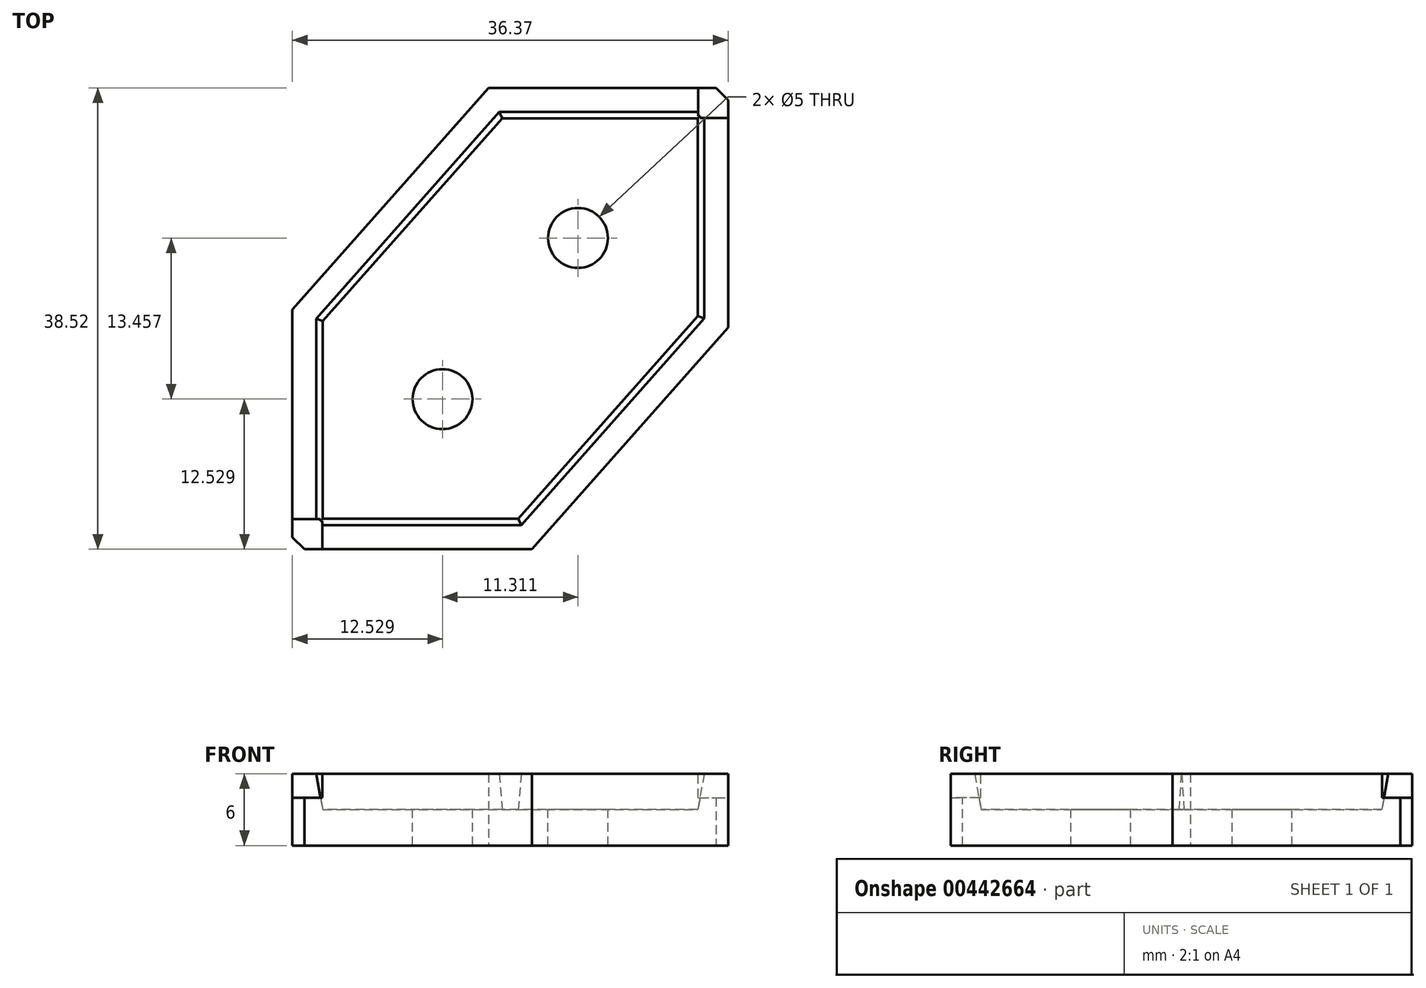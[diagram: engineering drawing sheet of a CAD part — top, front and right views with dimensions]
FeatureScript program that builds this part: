
annotation { "Feature Type Name" : "Feature", "Feature Type Description" : "" }
export const myFeature = defineFeature(function(context is Context, id is Id, definition is map)
    precondition{}
    {
        {
            var Q0;
            Q0=qCreatedBy(makeId("Top.planeOp"),FACE);
            var sketch = newSketch(context, id + "F0", { "sketchPlane" : qUnion([Q0])});
            skLineSegment(sketch, "E0.bottom", {"start": v(0, 0) * mm, "end": v(20, 0) * mm});
            skLineSegment(sketch, "E0.top", {"start": v(16.37, 38.52) * mm, "end": v(36.37, 38.52) * mm});
            skLineSegment(sketch, "E0.left", {"start": v(0, 0) * mm, "end": v(0, 20) * mm});
            skLineSegment(sketch, "E0.right", {"start": v(36.37, 18.52) * mm, "end": v(36.37, 38.52) * mm});
            skLineSegment(sketch, "E1", {"start": v(16.37, 38.52) * mm, "end": v(0, 20) * mm});
            skLineSegment(sketch, "E2", {"start": v(36.37, 18.52) * mm, "end": v(20, 0) * mm});
            skSolve(sketch);
        }
        {
            var Q0;
            Q0=qSketchRegion(id+"F0",true);
            extrude(context, id + "F1", {"entities" : qUnion([Q0]), "depth" : 6 * mm});
        }
        {
            var Q0;
            Q0=makeQuery(id+"F1.opExtrude","CAP_FACE",FACE,{"disambiguationData":[OSD([sQuery(id+"F0.wireOp",EDGE,"E0.bottom"),sQuery(id+"F0.wireOp",EDGE,"E0.top"),sQuery(id+"F0.wireOp",EDGE,"E0.left"),sQuery(id+"F0.wireOp",EDGE,"E0.right"),sQuery(id+"F0.wireOp",EDGE,"E1"),sQuery(id+"F0.wireOp",EDGE,"E2")])],"isStart":false});
            var sketch = newSketch(context, id + "F2", { "sketchPlane" : qUnion([Q0])});
            skLineSegment(sketch, "E3.bottom", {"start": v(2, 2) * mm, "end": v(19.1, 2) * mm});
            skLineSegment(sketch, "E3.top", {"start": v(17.27, 36.52) * mm, "end": v(34.37, 36.52) * mm});
            skLineSegment(sketch, "E3.left", {"start": v(2, 2) * mm, "end": v(2, 19.24) * mm});
            skLineSegment(sketch, "E3.right", {"start": v(34.37, 19.27) * mm, "end": v(34.37, 36.52) * mm});
            skLineSegment(sketch, "E4", {"start": v(17.27, 36.52) * mm, "end": v(2, 19.24) * mm});
            skLineSegment(sketch, "E5", {"start": v(34.37, 19.27) * mm, "end": v(19.1, 2) * mm});
            skSolve(sketch);
        }
        {
            var Q0;
            Q0 = qSketchRegion(id + "F2", true);
            extrude(context, id + "F3", {"entities" : qUnion([Q0]), "operationType" : NewBodyOperationType.REMOVE, "oppositeDirection" : true, "depth" : 3 * mm, "hasDraft" : true, "draftAngle" : 10 * degree, "draftPullDirection" : true});
        }
        {
            var Q0;
            Q0=makeQuery(id+"F1.opExtrude","SWEPT_EDGE",EDGE,{"disambiguationData":[OSD([sQuery(id+"F0.wireOp",EDGE,"E0.bottom"),sQuery(id+"F0.wireOp",EDGE,"E0.left")])]});
            var Q1;
            Q1=makeQuery(id+"F1.opExtrude","SWEPT_EDGE",EDGE,{"disambiguationData":[OSD([sQuery(id+"F0.wireOp",EDGE,"E0.top"),sQuery(id+"F0.wireOp",EDGE,"E0.right")])]});
            chamfer(context, id + "F4", {"entities" : qUnion([Q0, Q1]), "width" : 1 * mm});
        }
        {
            var Q0;
            Q0=makeQuery(id+"F1.opExtrude","CAP_FACE",FACE,{"disambiguationData":[OSD([sQuery(id+"F0.wireOp",EDGE,"E0.bottom"),sQuery(id+"F0.wireOp",EDGE,"E0.top"),sQuery(id+"F0.wireOp",EDGE,"E0.left"),sQuery(id+"F0.wireOp",EDGE,"E0.right")])],"isStart":false});
            var sketch = newSketch(context, id + "F5", { "sketchPlane" : qUnion([Q0])});
            skLineSegment(sketch, "E6.bottom", {"start": v(0, 2.5) * mm, "end": v(2.5, 2.5) * mm});
            skLineSegment(sketch, "E6.top", {"start": v(0, 0) * mm, "end": v(2.5, 0) * mm});
            skLineSegment(sketch, "E6.left", {"start": v(0, 2.5) * mm, "end": v(0, 0) * mm});
            skLineSegment(sketch, "E6.right", {"start": v(2.5, 2.5) * mm, "end": v(2.5, 0) * mm});
            skLineSegment(sketch, "E7.bottom", {"start": v(33.87, 38.52) * mm, "end": v(36.37, 38.52) * mm});
            skLineSegment(sketch, "E7.top", {"start": v(33.87, 36.02) * mm, "end": v(36.37, 36.02) * mm});
            skLineSegment(sketch, "E7.left", {"start": v(36.37, 38.52) * mm, "end": v(36.37, 36.02) * mm});
            skLineSegment(sketch, "E7.right", {"start": v(33.87, 38.52) * mm, "end": v(33.87, 36.02) * mm});
            skSolve(sketch);
        }
        {
            var Q0;
            Q0 = qSketchRegion(id + "F5", true);
            extrude(context, id + "F6", {"entities" : qUnion([Q0]), "operationType" : NewBodyOperationType.REMOVE, "oppositeDirection" : true, "depth" : 2 * mm});
        }
        {
            var Q0;
            Q0=makeQuery(id+"F3.boolean.opBoolean","COPY",FACE,{"derivedFrom":makeQuery(id+"F3.opExtrude","CAP_FACE",FACE,{"disambiguationData":[OSD([sQuery(id+"F2.wireOp",EDGE,"E3.bottom"),sQuery(id+"F2.wireOp",EDGE,"E3.top"),sQuery(id+"F2.wireOp",EDGE,"E3.left"),sQuery(id+"F2.wireOp",EDGE,"E3.right"),sQuery(id+"F2.wireOp",EDGE,"E4"),sQuery(id+"F2.wireOp",EDGE,"E5")])],"isStart":false})});
            var sketch = newSketch(context, id + "F7", { "sketchPlane" : qUnion([Q0])});
            skCircle(sketch, "E8", {"center": v(12.53, 12.53) * mm, "radius": 2.5 * mm});
            skCircle(sketch, "E9", {"center": v(23.84, 25.99) * mm, "radius": 2.5 * mm});
            skSolve(sketch);
        }
        {
            var Q0;
            Q0 = qSketchRegion(id + "F7", true);
            extrude(context, id + "F8", {"entities" : qUnion([Q0]), "operationType" : NewBodyOperationType.REMOVE, "endBound" : BoundingType.UP_TO_NEXT, "oppositeDirection" : true, "depth" : 25 * mm});
        }
    });
